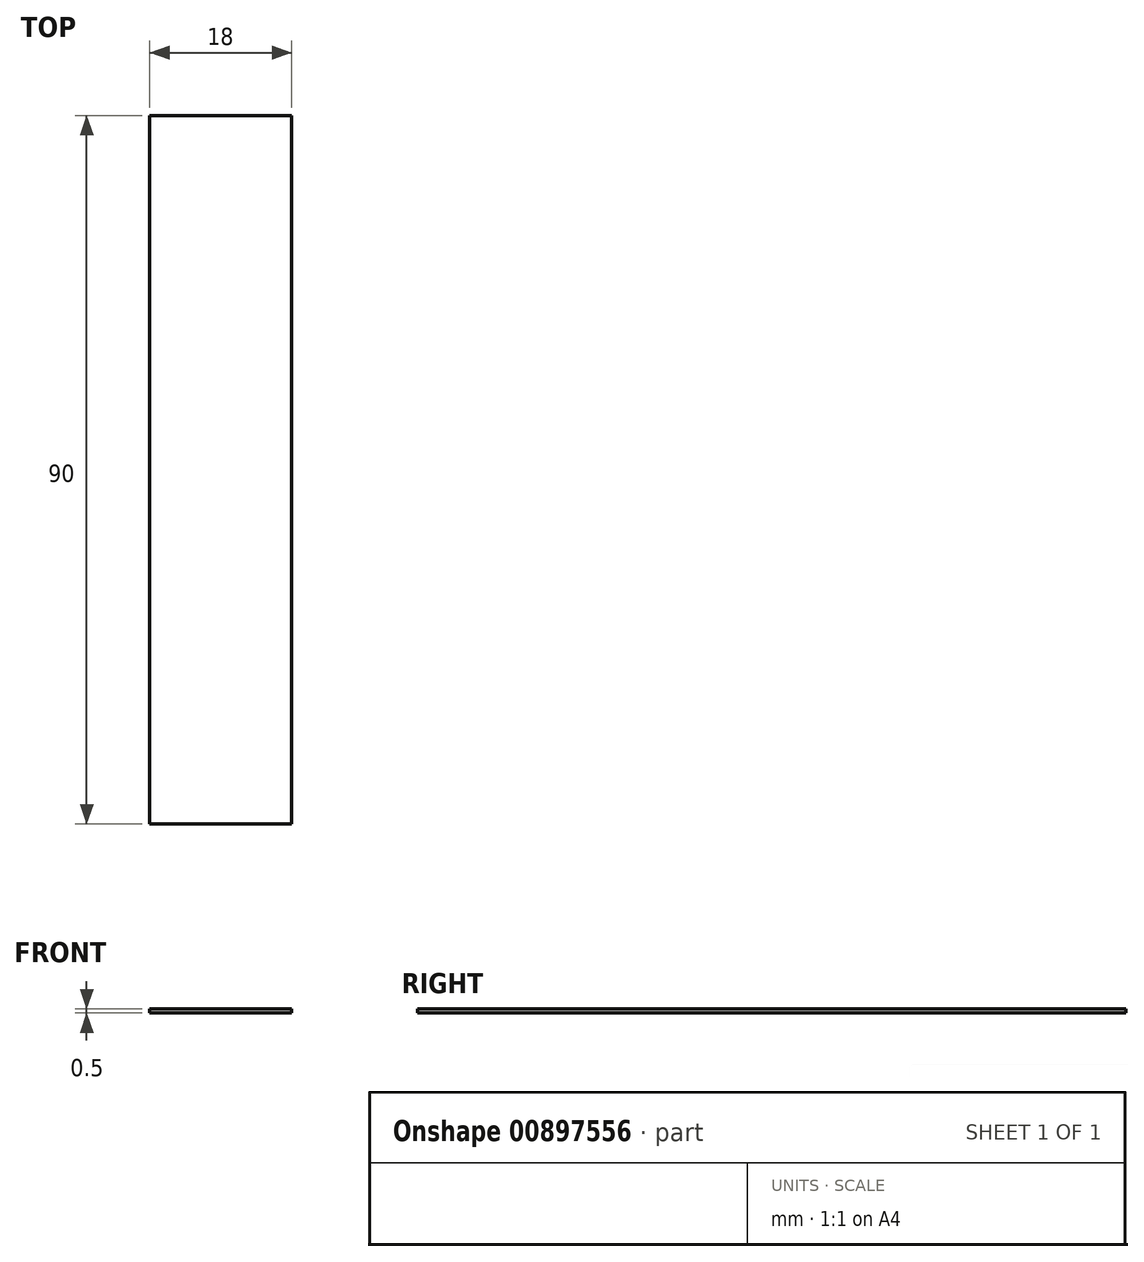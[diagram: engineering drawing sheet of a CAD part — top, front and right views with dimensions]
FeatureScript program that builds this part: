
annotation { "Feature Type Name" : "Feature", "Feature Type Description" : "" }
export const myFeature = defineFeature(function(context is Context, id is Id, definition is map)
    precondition{}
    {
        {
            var Q0;
            Q0=qCreatedBy(makeId("Top.planeOp"),FACE);
            var sketch = newSketch(context, id + "F0", { "sketchPlane" : qUnion([Q0])});
            skLineSegment(sketch, "E0.bottom", {"start": v(-15.03, 52.8) * mm, "end": v(2.97, 52.8) * mm});
            skLineSegment(sketch, "E0.top", {"start": v(-15.03, -37.2) * mm, "end": v(2.97, -37.2) * mm});
            skLineSegment(sketch, "E0.left", {"start": v(-15.03, 52.8) * mm, "end": v(-15.03, -37.2) * mm});
            skLineSegment(sketch, "E0.right", {"start": v(2.97, 52.8) * mm, "end": v(2.97, -37.2) * mm});
            skSolve(sketch);
        }
        {
            var Q0;
            Q0 = qSketchRegion(id + "F0", true);
            extrude(context, id + "F1", {"entities" : qUnion([Q0]), "depth" : 0.5 * mm, "offsetDistance" : 25 * mm});
        }
    });
